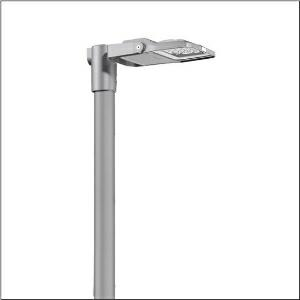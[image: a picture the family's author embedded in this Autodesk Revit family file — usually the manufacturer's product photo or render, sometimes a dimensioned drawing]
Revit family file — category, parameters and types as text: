
# Revit family: floodlight_fl_21_micro___pl64_5xa7762a2e3a_5d7d
name_source: partatom
category: Lighting Fixtures
units: mm (PartAtom-declared; Revit-internal decimal feet)

## family parameters
Cut with Voids When Loaded = No
Host = Face
Light Source = No
Part Type = Normal
Room Calculation Point = No
Round Connector Dimension = Use Diameter
Shared = No

## types (1)
- --- (1 x LED, 2870 lm, 23.1 W, 3000K)
    Apparent Load = 23 VA
    CIE Flux Codes = 28 80 98 100 100
    Color Rendering = 70
    Color Temperature = 3000K
    Default Elevation = 1800 mm
    Description = Floodlight FL 21 micro, floodlight, primary light control with lens, of PMMA, primary optical cover: protective disc, of toughened safety glass, transparent, light distribution: PL64, light emission: direct distribution, installation type: surface-mounted, LED, High Power LED, rated luminous flux: 2.870lm, luminous efficacy: 124lm/W, light colour: 730, colour temperature: 3000K, control gear: ECG iQ, control: Auto-Match, Temp-Guard, Night-Set, Smart-Wire, Desk-Remote (wireless, voltage-free reading and setting of iQ features in the workshop via application-optimized NFC function/RFID function), optimised constant luminous flux control (CLO 2.0), Street-Remote, with terminal, 6-pole, mains connection: 220..240V, AC, 50/60Hz, start of lifetime: 23W, end of lifetime: 24W, reduction: 11W, luminaire housing, of diecast aluminium, powder-coated, Siteco® metallic grey (DB 702S), corrosivity category C5 according to DIN EN ISO 12944, mast bracket, of steel, galvanised, powder-coated, Siteco® metallic grey (DB 702S), protection rating (complete): IP66, insulation class (complete): insulation class II (safety insulation), certification: CE, protection symbol: D, impact resistance: IK07, permissible operating ambient temperature: -40..+40°C, permissible operating ambient temperature for outdoor applications: -40..+50°C, standard: DIN EN 12944, packaging unit: 1 piece

Light Distribution: PL64
    Height = 65 mm
    Lamp = 1 x LED
    Lamp Light Flux = 2870 lm
    Lamp Power = 23.1 W
    Lamp count = 1
    Length = 312 mm
    Luminous efficacy = 124 lm/W
    Manufacturer = Siteco
    ModVariant = No
    Model = 5XA7762A2E3A
    Number of Poles = 1
    OnlyDefault = Yes
    Power Factor = 1
    Product Name = Floodlight FL 21 micro | PL64
    Product group = floodlight | pylon top
    ProductGroupID = 6101
    Protection Class = Protection class II
    Protection Degree = IP 66
    RLX_Detail_Level = 1
    RlxData = <blob elided: 101549 chars, md5=ff071377>
    Socket = socket
    Standby Power = 0 W
    System Light Flux = 2870 lm
    System Power = 23 W
    Type Comments = factory setting: luminous flux: 100 % | dim-lin: 254 | 455 mA
    Type Image = l_1007121.jpg
    URL = http://relux.com
    VarID = @adj_094167
    Voltage = 0 V
    Weight = 0.00 kg
    Width = 230 mm

## geometry (parser evidence)
native form markers: Blend x4, Sweep x12
no freeform markers — native parametric forms only
